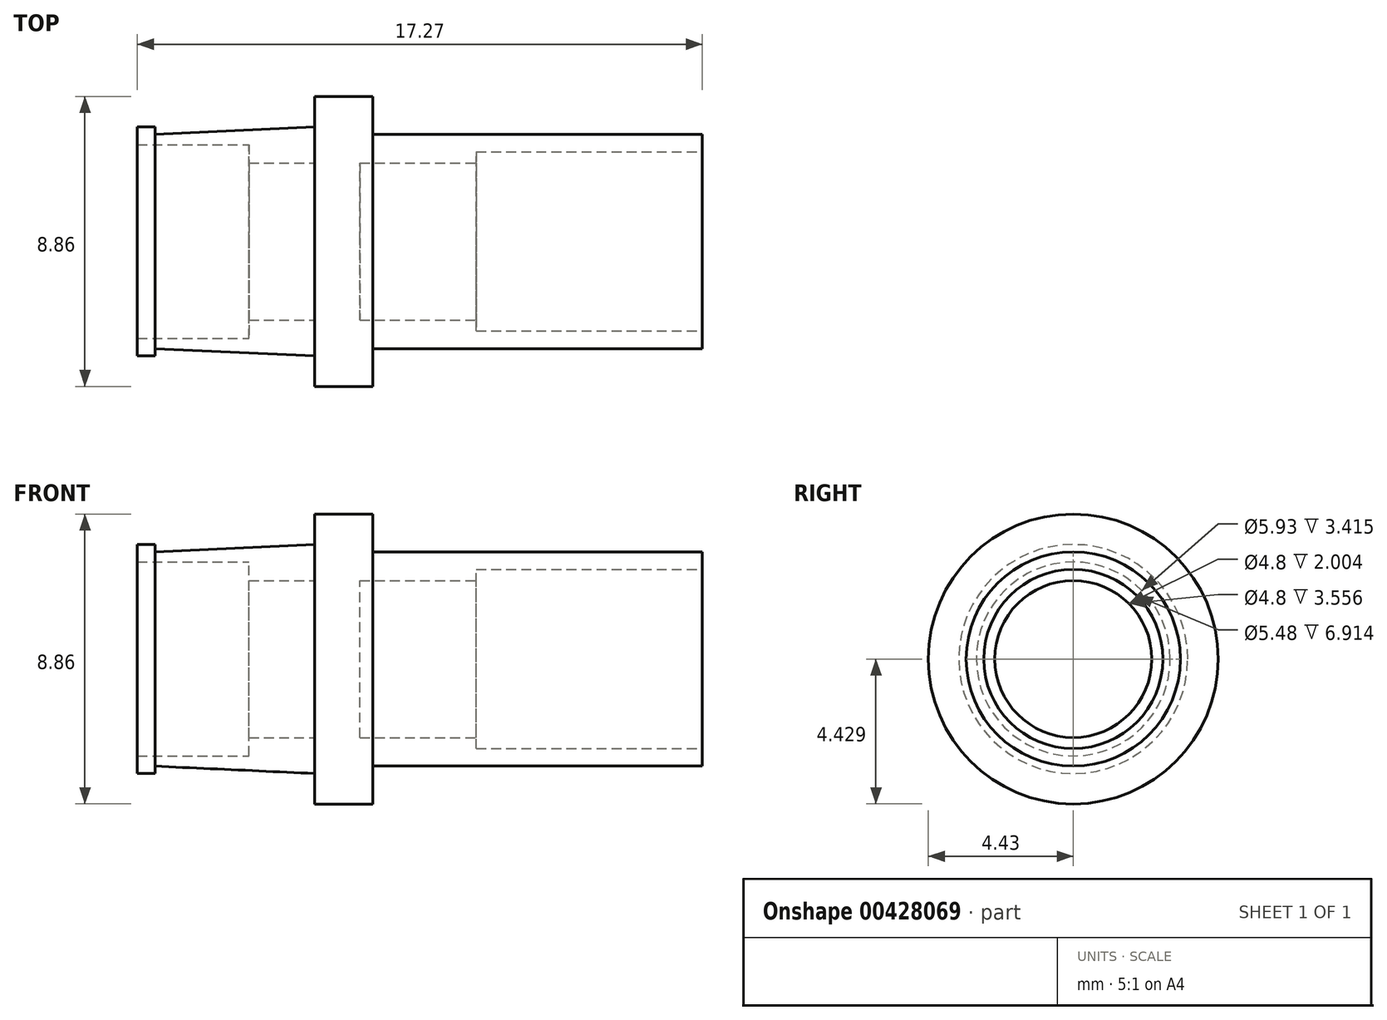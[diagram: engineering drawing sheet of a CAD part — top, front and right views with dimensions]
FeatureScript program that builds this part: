
annotation { "Feature Type Name" : "Feature", "Feature Type Description" : "" }
export const myFeature = defineFeature(function(context is Context, id is Id, definition is map)
    precondition{}
    {
        {
            var Q0;
            Q0=qCreatedBy(makeId("Front.planeOp"),FACE);
            var sketch = newSketch(context, id + "F0", { "sketchPlane" : qUnion([Q0])});
            skLineSegment(sketch, "E0", {"start": v(0, 0) * mm, "end": v(1.78, 0) * mm});
            skLineSegment(sketch, "E1", {"start": v(1.78, 0) * mm, "end": v(1.78, -1.16) * mm});
            skLineSegment(sketch, "E2", {"start": v(1.78, -1.16) * mm, "end": v(11.85, -1.16) * mm});
            skLineSegment(sketch, "E3", {"start": v(11.85, -1.16) * mm, "end": v(11.85, -1.7) * mm});
            skLineSegment(sketch, "E4", {"start": v(11.85, -1.7) * mm, "end": v(4.94, -1.7) * mm});
            skLineSegment(sketch, "E5", {"start": v(4.94, -1.7) * mm, "end": v(4.94, -2.03) * mm});
            skLineSegment(sketch, "E6", {"start": v(4.94, -2.03) * mm, "end": v(1.38, -2.03) * mm});
            skLineSegment(sketch, "E7", {"start": v(1.38, -2.03) * mm, "end": v(1.38, -4.43) * mm});
            skLineSegment(sketch, "E8", {"start": v(1.38, -4.43) * mm, "end": v(0, -4.43) * mm});
            skLineSegment(sketch, "E9", {"start": v(0, -4.43) * mm, "end": v(0, -2.03) * mm});
            skLineSegment(sketch, "E10", {"start": v(0, -2.03) * mm, "end": v(-2, -2.03) * mm});
            skLineSegment(sketch, "E11", {"start": v(-2, -2.03) * mm, "end": v(-2, -1.47) * mm});
            skLineSegment(sketch, "E12", {"start": v(-2, -1.47) * mm, "end": v(-5.42, -1.47) * mm});
            skLineSegment(sketch, "E13", {"start": v(-5.42, -1.47) * mm, "end": v(-5.42, -0.93) * mm});
            skLineSegment(sketch, "E14", {"start": v(-5.42, -0.93) * mm, "end": v(-4.88, -0.93) * mm});
            skLineSegment(sketch, "E15", {"start": v(-4.88, -0.93) * mm, "end": v(-4.88, -1.16) * mm});
            skLineSegment(sketch, "E16", {"start": v(-4.88, -1.16) * mm, "end": v(0, -0.93) * mm});
            skLineSegment(sketch, "E17", {"start": v(0, -0.93) * mm, "end": v(0, 0) * mm});
            skSolve(sketch);
        }
        {
            var Q0;
            Q0=makeQuery(id+"F0.imprint","IMPRINT",FACE,{"disambiguationData":[TD([[makeQuery(id+"F0.imprint","IMPRINT",EDGE,{"derivedFrom":sQuery(id+"F0.wireOp",EDGE,"E0")}),-1.0]])]});
            var Q1;
            Q1=sQuery(id+"F0.wireOp",EDGE,"E8");
            revolve(context, id + "F1", {"entities" : qUnion([Q0]), "axis" : qUnion([Q1]), "revolveType" : RevolveType.FULL});
        }
    });
